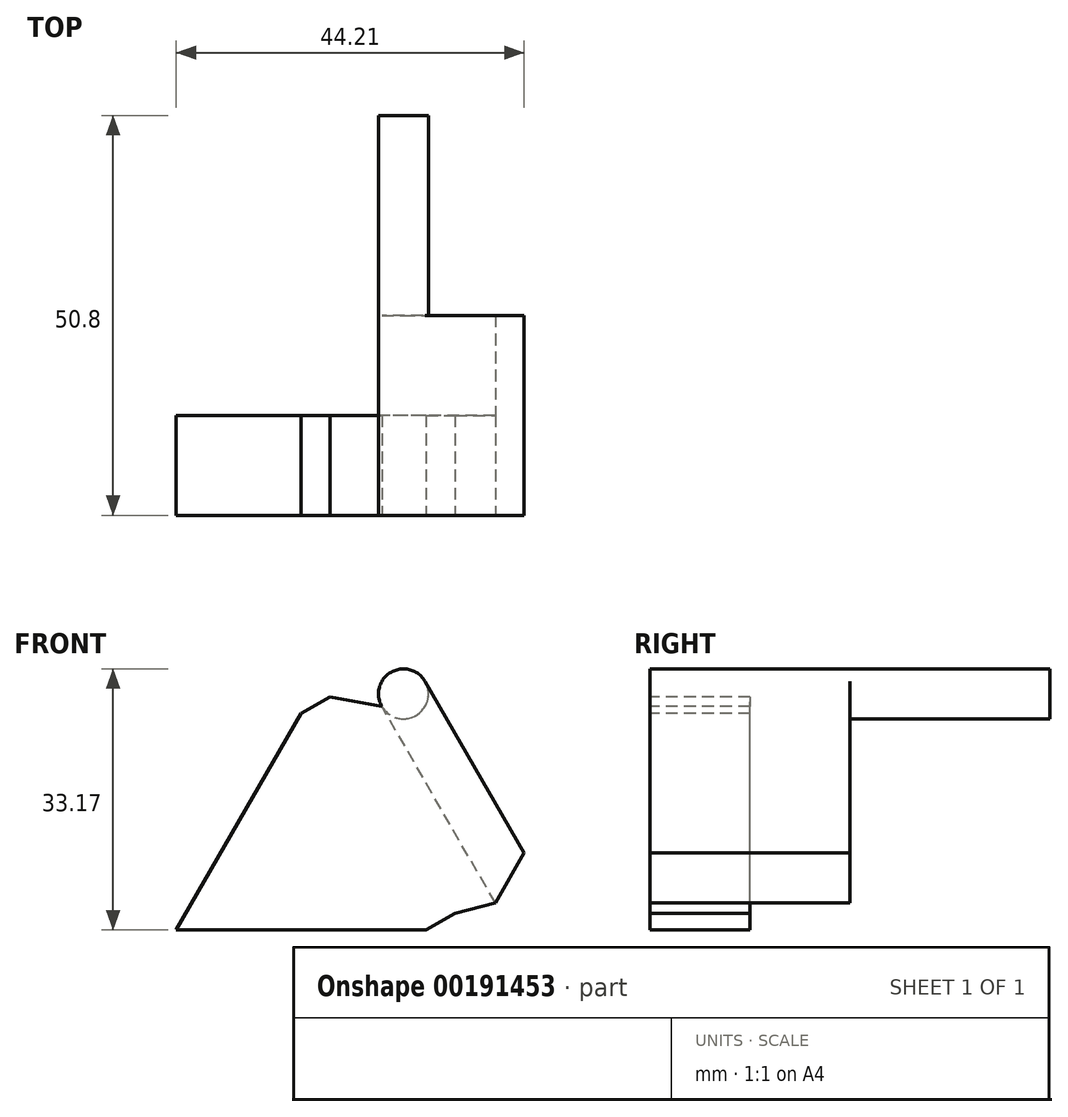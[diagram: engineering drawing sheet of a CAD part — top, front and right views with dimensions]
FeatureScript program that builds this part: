
annotation { "Feature Type Name" : "Feature", "Feature Type Description" : "" }
export const myFeature = defineFeature(function(context is Context, id is Id, definition is map)
    precondition{}
    {
        {
            var Q0;
            Q0=qCreatedBy(makeId("Front.planeOp"),FACE);
            var sketch = newSketch(context, id + "F0", { "sketchPlane" : qUnion([Q0])});
            skPoint(sketch, "E0", {"position": v(-37.38, 23.03) * mm});
            skLineSegment(sketch, "E1", {"start": v(36.3, -22.73) * mm, "end": v(32.62, -29.08) * mm});
            skLineSegment(sketch, "E2", {"start": v(32.62, -29.08) * mm, "end": v(18.2, -4.1) * mm});
            skLineSegment(sketch, "E3", {"start": v(36.3, -22.73) * mm, "end": v(23.7, -0.93) * mm});
            skPoint(sketch, "E4", {"position": v(22.54, -5.26) * mm});
            skPoint(sketch, "E5", {"position": v(20.96, -2.51) * mm});
            skCircle(sketch, "E6", {"center": v(20.96, -2.51) * mm, "radius": 3.17 * mm});
            skPoint(sketch, "E7", {"position": v(-7.92, -32.5) * mm});
            skPoint(sketch, "E8", {"position": v(7.95, -5.01) * mm});
            skPoint(sketch, "E9", {"position": v(11.64, -2.88) * mm});
            skPoint(sketch, "E10", {"position": v(23.83, -32.5) * mm});
            skPoint(sketch, "E11", {"position": v(27.51, -30.38) * mm});
            skLineSegment(sketch, "E12", {"start": v(-7.92, -32.5) * mm, "end": v(7.95, -5.01) * mm});
            skLineSegment(sketch, "E13", {"start": v(7.95, -5.01) * mm, "end": v(11.64, -2.88) * mm});
            skLineSegment(sketch, "E14", {"start": v(23.83, -32.5) * mm, "end": v(-7.92, -32.5) * mm});
            skLineSegment(sketch, "E15", {"start": v(23.83, -32.5) * mm, "end": v(27.51, -30.38) * mm});
            skLineSegment(sketch, "E16", {"start": v(27.51, -30.38) * mm, "end": v(11.64, -2.88) * mm});
            skLineSegment(sketch, "E17", {"start": v(27.51, -30.38) * mm, "end": v(32.62, -29.08) * mm});
            skLineSegment(sketch, "E18", {"start": v(11.64, -2.88) * mm, "end": v(18.2, -4.1) * mm});
            skPoint(sketch, "E19", {"position": v(34.46, -25.9) * mm});
            skSolve(sketch);
        }
        {
            var Q0;
            Q0=makeQuery(id+"F0.imprint","IMPRINT",FACE,{"disambiguationData":[TD([[makeQuery(id+"F0.imprint","IMPRINT",EDGE,{"derivedFrom":sQuery(id+"F0.wireOp",EDGE,"E12")}),-1.0]])]});
            var Q1;
            Q1=makeQuery(id+"F0.imprint","IMPRINT",FACE,{"disambiguationData":[TD([[makeQuery(id+"F0.imprint","IMPRINT",EDGE,{"derivedFrom":sQuery(id+"F0.wireOp",EDGE,"E2")}),1.0]])]});
            extrude(context, id + "F1", {"entities" : qUnion([Q0, Q1]), "oppositeDirection" : true, "depth" : 12.7 * mm});
        }
        {
            var Q0;
            Q0=makeQuery(id+"F0.imprint","IMPRINT",FACE,{"disambiguationData":[TD([[makeQuery(id+"F0.imprint","IMPRINT",EDGE,{"derivedFrom":sQuery(id+"F0.wireOp",EDGE,"E1")}),-1.0]])]});
            extrude(context, id + "F2", {"entities" : qUnion([Q0]), "operationType" : NewBodyOperationType.ADD, "oppositeDirection" : true, "depth" : 25.4 * mm});
        }
        {
            var Q0;
            {var subQ0=sQuery(id+"F0.wireOp",EDGE,"E6");var subQ2=makeQuery(id+"F0.imprint","INTERSECT",VERTEX,{"derivedFrom":[sQuery(id+"F0.wireOp",EDGE,"E3"),subQ0]});Q0=makeQuery(id+"F0.imprint","IMPRINT",FACE,{"disambiguationData":[TD([[makeQuery(id+"F0.imprint","IMPRINT",EDGE,{"disambiguationData":[TD([[subQ2,-1.0]])],"derivedFrom":subQ0}),1.0]])]});}
            extrude(context, id + "F3", {"entities" : qUnion([Q0]), "operationType" : NewBodyOperationType.ADD, "oppositeDirection" : true, "depth" : 50.8 * mm});
        }
    });
